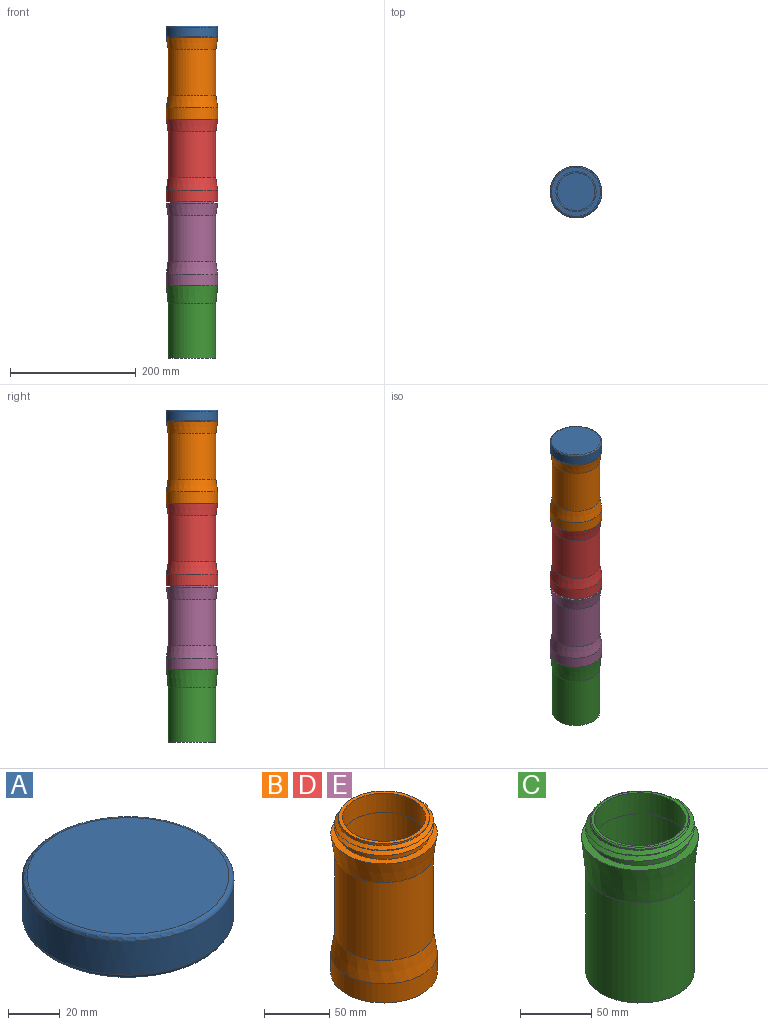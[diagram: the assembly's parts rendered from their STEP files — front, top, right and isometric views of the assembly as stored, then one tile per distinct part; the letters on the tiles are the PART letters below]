
ASSEMBLY  parts=5 mates=4
PART A: 16 faces, bbox 88.8x90.1x20 mm
  f0: plane 60x60mm, normal (0,0,-1), area 2827.4mm2, adj f1
  f1: cylinder r=30mm len=60mm, axis (0,0,1), area 188.5mm2, adj f0,f2
  f2: torus R=31mm, axis (0,0,1), area 611.9mm2, adj f1,f3
  f3: cylinder r=32mm len=64mm, axis (0,0,1), area 201.1mm2, adj f2,f4
  f4: plane 78x78mm, normal (0,0,-1), area 1561.4mm2, adj f3,f7
  f5: cylinder r=39mm len=78mm, axis (0,0,1), area 612.6mm2, adj f6,f10,f13,f14
  f6: cylinder r=39mm len=78mm, axis (0,0,1), area 122.5mm2, adj f5,f7,f12,f13
  f7: cylinder r=39mm len=78mm, axis (0,0,1), area 1470.3mm2, adj f4,f6,f11,f12
  f8: cylinder r=41mm len=82mm, axis (0,0,1), area 4121.8mm2, adj f14,f15
  f9: plane 78x78mm, normal (0,0,1), area 4778.4mm2, adj f15
  f10: plane 4.5x3mm, normal (0,-1,0), area 6.8mm2, adj f5,f12,f13
  f11: plane 4.5x3mm, normal (0,1,0), area 6.8mm2, adj f7,f12,f13
  f12: bspline ~90.07x78mm, area 1767.4mm2, adj f6,f7,f10,f11,f13
  f13: bspline ~90.07x78mm, area 1767.7mm2, adj f5,f6,f10,f11,f12
  f14: torus R=39mm, axis (0,0,1), area 795mm2, adj f5,f8
  f15: torus R=39mm, axis (0,0,-1), area 795mm2, adj f8,f9
PART B: 29 faces, bbox 82x87.8x146 mm
  f0: cylinder r=35mm len=70mm, axis (0,0,1), area 659.7mm2, adj f1,f7,f26,f28
  f1: cylinder r=35mm len=70mm, axis (0,0,1), area 110mm2, adj f0,f2,f27,f28
  f2: cylinder r=35mm len=70mm, axis (0,0,1), area 549.8mm2, adj f1,f8,f25,f27
  f3: cylinder r=41mm len=82mm, axis (0,0,1), area 4637mm2, adj f4,f20
  f4: cone r=41mm half-angle=8.6deg, axis (0,0,-1), area 4963.7mm2, adj f3,f5
  f5: cylinder r=38mm len=76mm, axis (0,0,1), area 17537.6mm2, adj f4,f6
  f6: cone r=41mm half-angle=8.6deg, axis (0,0,1), area 4963.7mm2, adj f5,f7
  f7: plane 82x82mm, normal (0,0,1), area 1432.6mm2, adj f0,f6
  f8: plane 70x70mm, normal (0,0,1), area 631.5mm2, adj f2,f9
  f9: cylinder r=32mm len=64mm, axis (0,0,1), area 3619.1mm2, adj f8,f10
  f10: plane 70x70mm, normal (0,0,-1), area 631.5mm2, adj f9,f11
  f11: cylinder r=35mm len=110mm, axis (0,0,1), area 24190.3mm2, adj f10,f12
  f12: plane 70x70mm, normal (0,0,1), area 1021mm2, adj f11,f13
  f13: cylinder r=30mm len=60mm, axis (0,0,1), area 754mm2, adj f12,f14
  f14: torus R=31mm, axis (0,0,1), area 611.9mm2, adj f13,f15
  f15: cylinder r=32mm len=64mm, axis (0,0,1), area 201.1mm2, adj f14,f16
  f16: plane 76x76mm, normal (0,0,-1), area 1319.5mm2, adj f15,f17
  f17: cylinder r=38mm len=76mm, axis (0,0,1), area 596.9mm2, adj f16,f18,f21,f23
  f18: cylinder r=38mm len=76mm, axis (0,0,1), area 119.4mm2, adj f17,f19,f23,f24
  f19: cylinder r=38mm len=76mm, axis (0,0,1), area 716.3mm2, adj f18,f20,f22,f24
  f20: plane 82x82mm, normal (0,0,-1), area 744.6mm2, adj f3,f19
  f21: plane 4.5x3mm, normal (0,1,0), area 6.7mm2, adj f17,f23,f24
  f22: plane 4.5x3mm, normal (0,-1,0), area 6.7mm2, adj f19,f23,f24
  f23: bspline ~87.76x76mm, area 1720.6mm2, adj f17,f18,f21,f22,f24
  f24: bspline ~87.76x76mm, area 1720.3mm2, adj f18,f19,f21,f22,f23
  f25: plane 4.5x3mm, normal (0,1,0), area 6.7mm2, adj f2,f27,f28
  f26: plane 4.5x3mm, normal (0,-1,0), area 6.7mm2, adj f0,f27,f28
  f27: bspline ~87.76x76mm, area 1720.3mm2, adj f1,f2,f25,f26,f28
  f28: bspline ~87.76x76mm, area 1720.6mm2, adj f0,f1,f25,f26,f27
PART C: 17 faces, bbox 82.3x88.1x132.1 mm
  f0: cylinder r=38mm len=86.15mm, axis (0,0,-1), area 20569.4mm2, adj f1,f11
  f1: cone r=41mm half-angle=5.7deg, axis (0,0,1), area 7445.6mm2, adj f0,f2
  f2: plane 82x82mm, normal (0,0,1), area 1432.6mm2, adj f1,f3
  f3: cylinder r=35mm len=70mm, axis (0,0,-1), area 714.7mm2, adj f2,f4,f13,f14,f15
  f4: cylinder r=35mm len=70mm, axis (0,0,-1), area 357.2mm2, adj f3,f5,f12,f14,f15,f16
  f5: cylinder r=35mm len=45.5mm, axis (0,0,-1), area 49.3mm2, adj f4,f14,f16
  f6: plane 69.3x68.3mm, normal (0,0,1), area 430.9mm2, adj f7,f12,f14,f16
  f7: cylinder r=32mm len=64mm, axis (0,0,-1), area 3619.1mm2, adj f6,f8
  f8: plane 70x70mm, normal (0,0,-1), area 631.5mm2, adj f7,f9
  f9: cylinder r=35mm len=110mm, axis (0,0,-1), area 24190.3mm2, adj f8,f10
  f10: plane 70x70mm, normal (0,0,1), area 3848.5mm2, adj f9
  f11: plane 76x76mm, normal (0,0,-1), area 4536.5mm2, adj f0
  f12: plane 4.5x4mm, normal (0,1,0), area 7mm2, adj f4,f6,f14,f15,f16
  f13: plane 4.5x3mm, normal (0,-1,0), area 6.8mm2, adj f3,f14,f15
  f14: bspline ~87.76x76mm, area 1733.1mm2, adj f3,f4,f5,f6,f12,f13,f15,f16
  f15: bspline ~87.76x76mm, area 1720.6mm2, adj f3,f4,f12,f13,f14
  f16: torus R=34mm, axis (0,0,1), area 282.9mm2, adj f4,f5,f6,f12,f14
PART D: same geometry as B
PART E: same geometry as B
PLACE A rot(axis=(0,0,-1),20.2deg) t=(-1.69,24.86,526.61)mm
PLACE B rot(axis=(0,0,1),134.5deg) t=(-64.94,65.42,395.12)mm
PLACE C rot(axis=(0,0,-1),0deg) t=(-3.29,38.33,3.1)mm fixed
PLACE D rot(axis=(0,0,1),150.4deg) t=(-71.33,57.1,263.9)mm
PLACE E rot(axis=(0,0,-1),17.5deg) t=(-2.06,26.88,130.69)mm
MATE cylindrical D.f0 <-> E.f0  axis (0,0,-1) through (-38.29,38.33,248.9)mm
MATE cylindrical C.f0 <-> A.f1  axis (0,0,-1) through (-38.29,38.33,43.17)mm
MATE cylindrical E.f0 <-> C.f0  axis (0,0,-1) through (-38.29,38.33,115.69)mm
MATE cylindrical B.f0 <-> D.f0  axis (0,0,-1) through (-38.29,38.33,380.12)mm
